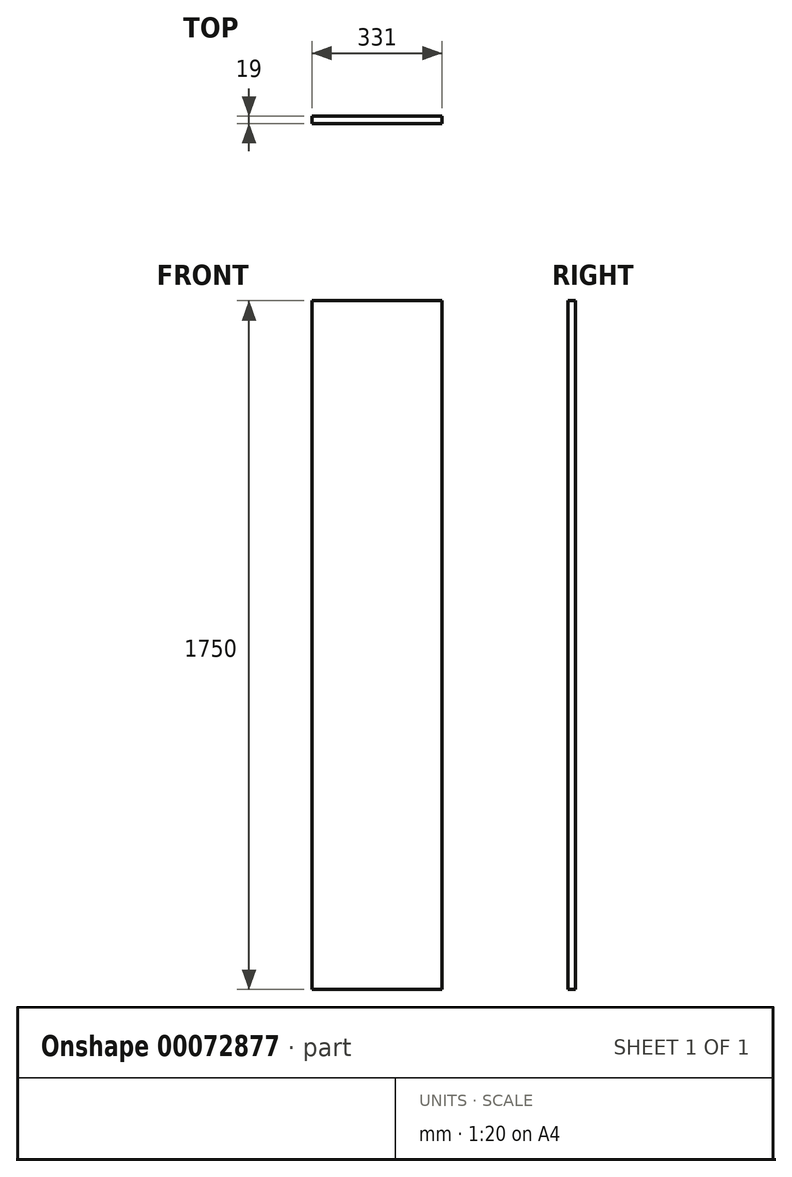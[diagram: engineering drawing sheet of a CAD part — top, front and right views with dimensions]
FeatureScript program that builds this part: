
annotation { "Feature Type Name" : "Feature", "Feature Type Description" : "" }
export const myFeature = defineFeature(function(context is Context, id is Id, definition is map)
    precondition{}
    {
        {
            var Q0;
            Q0=qCreatedBy(makeId("Front.planeOp"),FACE);
            var sketch = newSketch(context, id + "F0", { "sketchPlane" : qUnion([Q0])});
            skLineSegment(sketch, "E0.bottom", {"start": v(0, 0) * mm, "end": v(331, 0) * mm});
            skLineSegment(sketch, "E0.top", {"start": v(0, -1750) * mm, "end": v(331, -1750) * mm});
            skLineSegment(sketch, "E0.left", {"start": v(0, 0) * mm, "end": v(0, -1750) * mm});
            skLineSegment(sketch, "E0.right", {"start": v(331, 0) * mm, "end": v(331, -1750) * mm});
            skSolve(sketch);
        }
        {
            var Q0;
            Q0=qSketchRegion(id+"F0",true);
            extrude(context, id + "F1", {"entities" : qUnion([Q0]), "depth" : 19 * mm});
        }
    });
